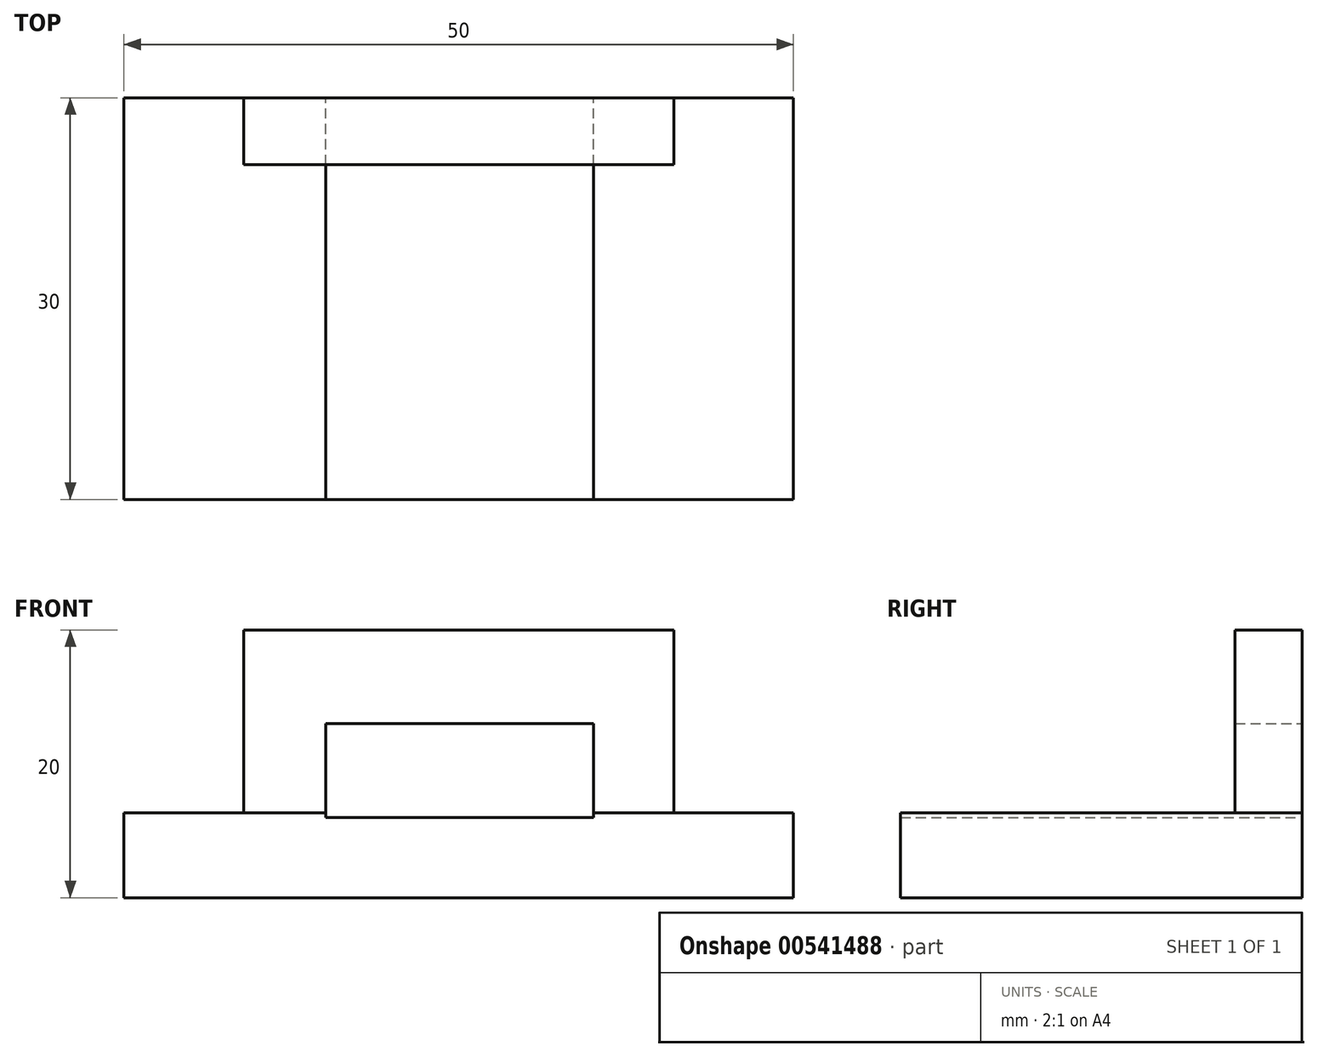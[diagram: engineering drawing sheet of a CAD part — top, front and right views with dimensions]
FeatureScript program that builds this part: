
annotation { "Feature Type Name" : "Feature", "Feature Type Description" : "" }
export const myFeature = defineFeature(function(context is Context, id is Id, definition is map)
    precondition{}
    {
        {
            var Q0;
            Q0=qCreatedBy(makeId("Front.planeOp"),FACE);
            var sketch = newSketch(context, id + "F0", { "sketchPlane" : qUnion([Q0])});
            skLineSegment(sketch, "E0.bottom", {"start": v(-15.87, 10.1) * mm, "end": v(16.27, 10.1) * mm});
            skLineSegment(sketch, "E0.top", {"start": v(-24.8, -9.9) * mm, "end": v(25.2, -9.9) * mm});
            skLineSegment(sketch, "E0.left", {"start": v(-24.8, -3.55) * mm, "end": v(-24.8, -9.9) * mm});
            skLineSegment(sketch, "E0.right", {"start": v(25.2, -3.55) * mm, "end": v(25.2, -9.9) * mm});
            skLineSegment(sketch, "E1", {"start": v(-24.8, -3.55) * mm, "end": v(-15.87, -3.55) * mm});
            skLineSegment(sketch, "E2", {"start": v(-15.87, -3.55) * mm, "end": v(-15.87, 10.1) * mm});
            skLineSegment(sketch, "E3", {"start": v(0.2, 10.1) * mm, "end": v(0.2, -9.9) * mm, "construction": true});
            skLineSegment(sketch, "E4.MirrorCS", {"start": v(16.27, -3.55) * mm, "end": v(16.27, 10.1) * mm});
            skLineSegment(sketch, "E5", {"start": v(16.27, -3.55) * mm, "end": v(25.2, -3.55) * mm});
            skLineSegment(sketch, "E6.bottom", {"start": v(-9.73, 3.1) * mm, "end": v(10.27, 3.1) * mm});
            skLineSegment(sketch, "E6.top", {"start": v(-9.73, -3.9) * mm, "end": v(10.27, -3.9) * mm});
            skLineSegment(sketch, "E6.left", {"start": v(-9.73, 3.1) * mm, "end": v(-9.73, -3.9) * mm});
            skLineSegment(sketch, "E6.right", {"start": v(10.27, 3.1) * mm, "end": v(10.27, -3.9) * mm});
            skSolve(sketch);
        }
        {
            var Q0;
            Q0 = qSketchRegion(id + "F0", true);
            extrude(context, id + "F1", {"entities" : qUnion([Q0]), "depth" : 5 * mm, "offsetDistance" : 25 * mm});
        }
        {
            var Q0;
            Q0=makeQuery(id+"F1.opExtrude","CAP_FACE",FACE,{"disambiguationData":[OSD([sQuery(id+"F0.wireOp",EDGE,"E0.bottom"),sQuery(id+"F0.wireOp",EDGE,"E0.top"),sQuery(id+"F0.wireOp",EDGE,"E0.left"),sQuery(id+"F0.wireOp",EDGE,"E0.right"),sQuery(id+"F0.wireOp",EDGE,"E1"),sQuery(id+"F0.wireOp",EDGE,"E2"),sQuery(id+"F0.wireOp",EDGE,"E4.MirrorCS"),sQuery(id+"F0.wireOp",EDGE,"E5"),sQuery(id+"F0.wireOp",EDGE,"E6.bottom"),sQuery(id+"F0.wireOp",EDGE,"E6.top"),sQuery(id+"F0.wireOp",EDGE,"E6.left"),sQuery(id+"F0.wireOp",EDGE,"E6.right")])],"isStart":false});
            var sketch = newSketch(context, id + "F2", { "sketchPlane" : qUnion([Q0])});
            skLineSegment(sketch, "E7.bottom", {"start": v(-24.8, -3.55) * mm, "end": v(25.2, -3.55) * mm});
            skLineSegment(sketch, "E7.top", {"start": v(-24.8, -9.9) * mm, "end": v(25.2, -9.9) * mm});
            skLineSegment(sketch, "E7.left", {"start": v(-24.8, -3.55) * mm, "end": v(-24.8, -9.9) * mm});
            skLineSegment(sketch, "E7.right", {"start": v(25.2, -3.55) * mm, "end": v(25.2, -9.9) * mm});
            skSolve(sketch);
        }
        {
            var Q0;
            Q0=makeQuery(id+"F2.imprint","IMPRINT",FACE,{"disambiguationData":[TD([[makeQuery(id+"F2.imprint","IMPRINT",EDGE,{"derivedFrom":sQuery(id+"F2.wireOp",EDGE,"E7.top")}),1.0]])]});
            extrude(context, id + "F3", {"entities" : qUnion([Q0]), "operationType" : NewBodyOperationType.ADD, "depth" : 25 * mm, "offsetDistance" : 25 * mm});
        }
    });
